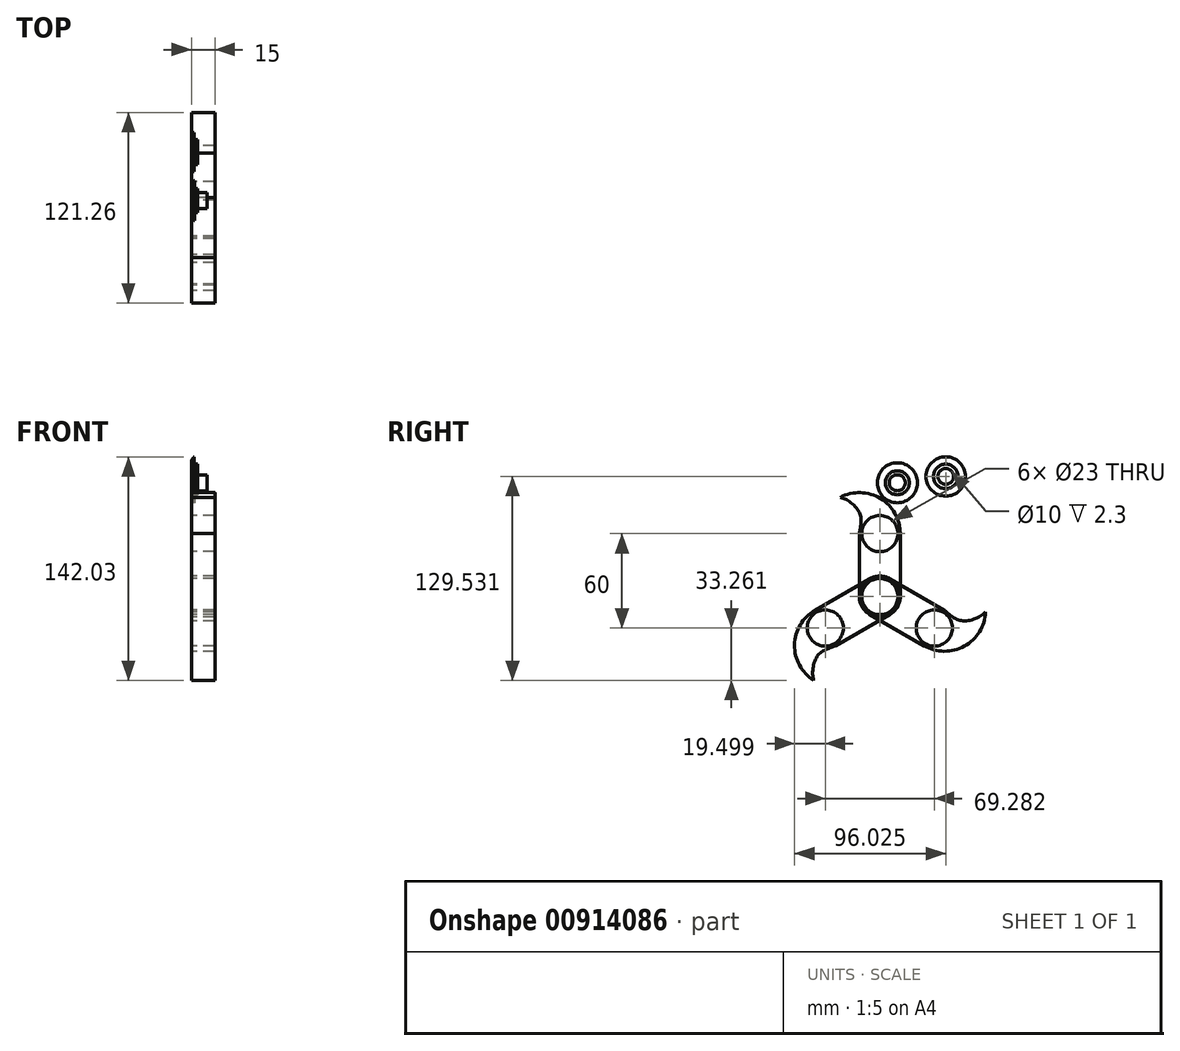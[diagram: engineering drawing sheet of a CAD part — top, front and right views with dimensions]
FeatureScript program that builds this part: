
annotation { "Feature Type Name" : "Feature", "Feature Type Description" : "" }
export const myFeature = defineFeature(function(context is Context, id is Id, definition is map)
    precondition{}
    {
        {
            var Q0;
            Q0=qCreatedBy(makeId("Right.planeOp"),FACE);
            var sketch = newSketch(context, id + "F0", { "sketchPlane" : qUnion([Q0])});
            skLineSegment(sketch, "E0.bottom", {"start": v(-26, 18.37) * mm, "end": v(0, 18.37) * mm});
            skLineSegment(sketch, "E0.top", {"start": v(-26, -21.63) * mm, "end": v(0, -21.63) * mm});
            skLineSegment(sketch, "E0.left", {"start": v(-26, 18.37) * mm, "end": v(-26, -21.63) * mm});
            skLineSegment(sketch, "E0.right", {"start": v(0, 18.37) * mm, "end": v(0, -21.63) * mm});
            skArc(sketch, "E1", {"start": v(0, 18.37) * mm, "mid": v(-13, 31.37) * mm, "end": v(-26, 18.37) * mm});
            skArc(sketch, "E2", {"start": v(-26, 18.37) * mm, "mid": v(-13, 5.37) * mm, "end": v(0, 18.37) * mm});
            skCircle(sketch, "E3", {"center": v(-13, -21.63) * mm, "radius": 13 * mm});
            skCircle(sketch, "E4", {"center": v(-13, 18.37) * mm, "radius": 11.5 * mm});
            skCircle(sketch, "E5", {"center": v(-13, -21.63) * mm, "radius": 11.5 * mm});
            skCircle(sketch, "E6", {"center": v(-26, 18.37) * mm, "radius": 26 * mm});
            skLineSegment(sketch, "E7", {"start": v(-26, 18.37) * mm, "end": v(-38.12, 41.37) * mm});
            skLineSegment(sketch, "E8.top", {"start": v(-26, -39.32) * mm, "end": v(0, -39.32) * mm});
            skLineSegment(sketch, "E8.left", {"start": v(-26, -21.63) * mm, "end": v(-26, -33.54) * mm});
            skLineSegment(sketch, "E8.right", {"start": v(0, -21.63) * mm, "end": v(0, -39.32) * mm});
            skFitSpline(sketch, "E9", {"points": [v(-38.12, 41.37) * mm, v(-26, 31.8) * mm, v(-26, 18.37) * mm], "startDerivative": vector(24.66, -5.43) * mm, "endDerivative": vector(-5.33, -29.42) * mm});
            skLineSegment(sketch, "E10", {"start": v(-31, -42.2) * mm, "end": v(-65.68, -62.23) * mm});
            skPoint(sketch, "E11.visualSharp", {"position": v(-26, -39.32) * mm});
            skArc(sketch, "E11.filletArc", {"start": v(-31, -42.2) * mm, "mid": v(-27.34, -38.54) * mm, "end": v(-26, -33.54) * mm});
            skLineSegment(sketch, "E12", {"start": v(-18.88, -39.32) * mm, "end": v(-36.21, -45.22) * mm});
            skSolve(sketch);
        }
        {
            var Q0;
            {var subQ1=sQuery(id+"F0.wireOp",EDGE,"E1");var subQ3=sQuery(id+"F0.wireOp",EDGE,"E9");var subQ4=makeQuery(id+"F0.imprint","INTERSECT",VERTEX,{"derivedFrom":[subQ1,subQ3]});Q0=makeQuery(id+"F0.imprint","IMPRINT",FACE,{"disambiguationData":[TD([[makeQuery(id+"F0.imprint","IMPRINT",EDGE,{"disambiguationData":[TD([[subQ4,1.0]])],"derivedFrom":subQ3}),1.0]])]});}
            var Q1;
            {var subQ0=sQuery(id+"F0.wireOp",EDGE,"E4");var subQ1=sQuery(id+"F0.wireOp",EDGE,"E0.bottom");var subQ2=makeQuery(id+"F0.imprint","INTERSECT",VERTEX,{"disambiguationData":[OD(0.0)],"derivedFrom":[subQ1,subQ0]});Q1=makeQuery(id+"F0.imprint","IMPRINT",FACE,{"disambiguationData":[TD([[makeQuery(id+"F0.imprint","IMPRINT",EDGE,{"disambiguationData":[TD([[subQ2,1.0]])],"derivedFrom":subQ0}),-1.0]])]});}
            var Q2;
            {var subQ0=sQuery(id+"F0.wireOp",EDGE,"E2");Q2=makeQuery(id+"F0.imprint","IMPRINT",FACE,{"disambiguationData":[TD([[makeQuery(id+"F0.imprint","IMPRINT",EDGE,{"derivedFrom":subQ0}),1.0]])]});}
            var Q3;
            {var subQ0=sQuery(id+"F0.wireOp",EDGE,"E2");Q3=makeQuery(id+"F0.imprint","IMPRINT",FACE,{"disambiguationData":[TD([[makeQuery(id+"F0.imprint","IMPRINT",EDGE,{"derivedFrom":subQ0}),-1.0]])]});}
            var Q4;
            {var subQ6=sQuery(id+"F0.wireOp",EDGE,"E0.right");Q4=makeQuery(id+"F0.imprint","IMPRINT",FACE,{"disambiguationData":[TD([[makeQuery(id+"F0.imprint","IMPRINT",EDGE,{"derivedFrom":subQ6}),-1.0]])]});}
            var Q5;
            {var subQ0=sQuery(id+"F0.wireOp",EDGE,"E0.top");var subQ4=sQuery(id+"F0.wireOp",EDGE,"E5");var subQ5=makeQuery(id+"F0.imprint","INTERSECT",VERTEX,{"disambiguationData":[OD(0.0)],"derivedFrom":[subQ4,subQ0]});Q5=makeQuery(id+"F0.imprint","IMPRINT",FACE,{"disambiguationData":[TD([[makeQuery(id+"F0.imprint","IMPRINT",EDGE,{"disambiguationData":[TD([[subQ5,1.0]])],"derivedFrom":subQ4}),-1.0]])]});}
            var Q6;
            {var subQ0=sQuery(id+"F0.wireOp",EDGE,"E0.top");var subQ4=sQuery(id+"F0.wireOp",EDGE,"E5");var subQ5=makeQuery(id+"F0.imprint","INTERSECT",VERTEX,{"disambiguationData":[OD(0.0)],"derivedFrom":[subQ4,subQ0]});Q6=makeQuery(id+"F0.imprint","IMPRINT",FACE,{"disambiguationData":[TD([[makeQuery(id+"F0.imprint","IMPRINT",EDGE,{"disambiguationData":[TD([[subQ5,-1.0]])],"derivedFrom":subQ4}),-1.0]])]});}
            extrude(context, id + "F1", {"entities" : qUnion([Q0, Q1, Q2, Q3, Q4, Q5, Q6]), "depth" : 15 * mm, "offsetDistance" : 25 * mm});
        }
        {
            var Q0;
            Q0=makeQuery(id+"F1.opExtrude","SWEPT_BODY",BODY,{"disambiguationData":[OSD([sQuery(id+"F0.wireOp",EDGE,"E0.left"),sQuery(id+"F0.wireOp",EDGE,"E0.right"),sQuery(id+"F0.wireOp",EDGE,"E3"),sQuery(id+"F0.wireOp",EDGE,"E4"),sQuery(id+"F0.wireOp",EDGE,"E5"),sQuery(id+"F0.wireOp",EDGE,"E6"),sQuery(id+"F0.wireOp",EDGE,"E9")])]});
            var Q1;
            Q1=makeQuery(id+"F1.opExtrude","SWEPT_FACE",FACE,{"disambiguationData":[OSD([sQuery(id+"F0.wireOp",EDGE,"E5")])]});
            circularPattern(context, id + "F2", {"entities" : qUnion([Q0]), "axis" : qUnion([Q1]), "angle" : 360 * degree, "instanceCount" : 3, "equalSpace" : true});
        }
        {
            var Q0;
            Q0=qCreatedBy(makeId("Right.planeOp"),FACE);
            var sketch = newSketch(context, id + "F3", { "sketchPlane" : qUnion([Q0])});
            skCircle(sketch, "E13", {"center": v(-1.88, 50.64) * mm, "radius": 12.7 * mm});
            skCircle(sketch, "E14", {"center": v(-1.88, 50.64) * mm, "radius": 7.62 * mm});
            skCircle(sketch, "E15", {"center": v(-1.88, 50.64) * mm, "radius": 5.08 * mm});
            skSolve(sketch);
        }
        {
            var Q0;
            Q0 = qSketchRegion(id + "F3", true);
            extrude(context, id + "F4", {"entities" : qUnion([Q0]), "depth" : 2 * mm, "offsetDistance" : 25.4 * mm});
        }
        {
            var Q0;
            Q0=makeQuery(id+"F3.imprint","IMPRINT",FACE,{"disambiguationData":[TD([[makeQuery(id+"F3.imprint","IMPRINT",EDGE,{"derivedFrom":sQuery(id+"F3.wireOp",EDGE,"E14")}),1.0]])]});
            extrude(context, id + "F5", {"entities" : qUnion([Q0]), "operationType" : NewBodyOperationType.ADD, "depth" : 4 * mm, "offsetDistance" : 25.4 * mm});
        }
        {
            var Q0;
            Q0=makeQuery(id+"F3.imprint","IMPRINT",FACE,{"disambiguationData":[TD([[makeQuery(id+"F3.imprint","IMPRINT",EDGE,{"derivedFrom":sQuery(id+"F3.wireOp",EDGE,"E15")}),1.0]])]});
            extrude(context, id + "F6", {"entities" : qUnion([Q0]), "operationType" : NewBodyOperationType.ADD, "depth" : 10 * mm, "offsetDistance" : 25.4 * mm});
        }
        {
            var Q0;
            Q0=makeQuery(id+"F4.opExtrude","CAP_EDGE",EDGE,{"disambiguationData":[OSD([sQuery(id+"F3.wireOp",EDGE,"E13")])],"isStart":true});
            fillet(context, id + "F7", {"entities" : qUnion([Q0]), "radius" : 5.08 * mm, "tangentPropagation" : true, "allowEdgeOverflow" : false});
        }
        {
            var Q0;
            Q0=qCreatedBy(makeId("Right.planeOp"),FACE);
            var sketch = newSketch(context, id + "F8", { "sketchPlane" : qUnion([Q0])});
            skCircle(sketch, "E16", {"center": v(28.89, 54.64) * mm, "radius": 12.5 * mm});
            skCircle(sketch, "E17", {"center": v(28.89, 54.64) * mm, "radius": 7.8 * mm});
            skCircle(sketch, "E18", {"center": v(28.89, 54.64) * mm, "radius": 5 * mm});
            skSolve(sketch);
        }
        {
            var Q0;
            Q0 = qSketchRegion(id + "F8", true);
            extrude(context, id + "F9", {"entities" : qUnion([Q0]), "depth" : 1.7 * mm, "offsetDistance" : 25 * mm});
        }
        {
            var Q0;
            Q0=makeQuery(id+"F8.imprint","IMPRINT",FACE,{"disambiguationData":[TD([[makeQuery(id+"F8.imprint","IMPRINT",EDGE,{"derivedFrom":sQuery(id+"F8.wireOp",EDGE,"E17")}),1.0]])]});
            extrude(context, id + "F10", {"entities" : qUnion([Q0]), "operationType" : NewBodyOperationType.ADD, "depth" : 4 * mm, "offsetDistance" : 25 * mm});
        }
        {
            var Q0;
            Q0=makeQuery(id+"F8.imprint","IMPRINT",FACE,{"disambiguationData":[TD([[makeQuery(id+"F8.imprint","IMPRINT",EDGE,{"derivedFrom":sQuery(id+"F8.wireOp",EDGE,"E18")}),1.0]])]});
            extrude(context, id + "F11", {"entities" : qUnion([Q0]), "operationType" : NewBodyOperationType.ADD, "depth" : 1.7 * mm, "offsetDistance" : 25 * mm});
        }
        {
            var Q0;
            Q0=makeQuery(id+"F9.opExtrude","CAP_EDGE",EDGE,{"disambiguationData":[OSD([sQuery(id+"F8.wireOp",EDGE,"E16")])],"isStart":true});
            fillet(context, id + "F12", {"entities" : qUnion([Q0]), "radius" : 5 * mm, "tangentPropagation" : true, "allowEdgeOverflow" : false});
        }
    });
